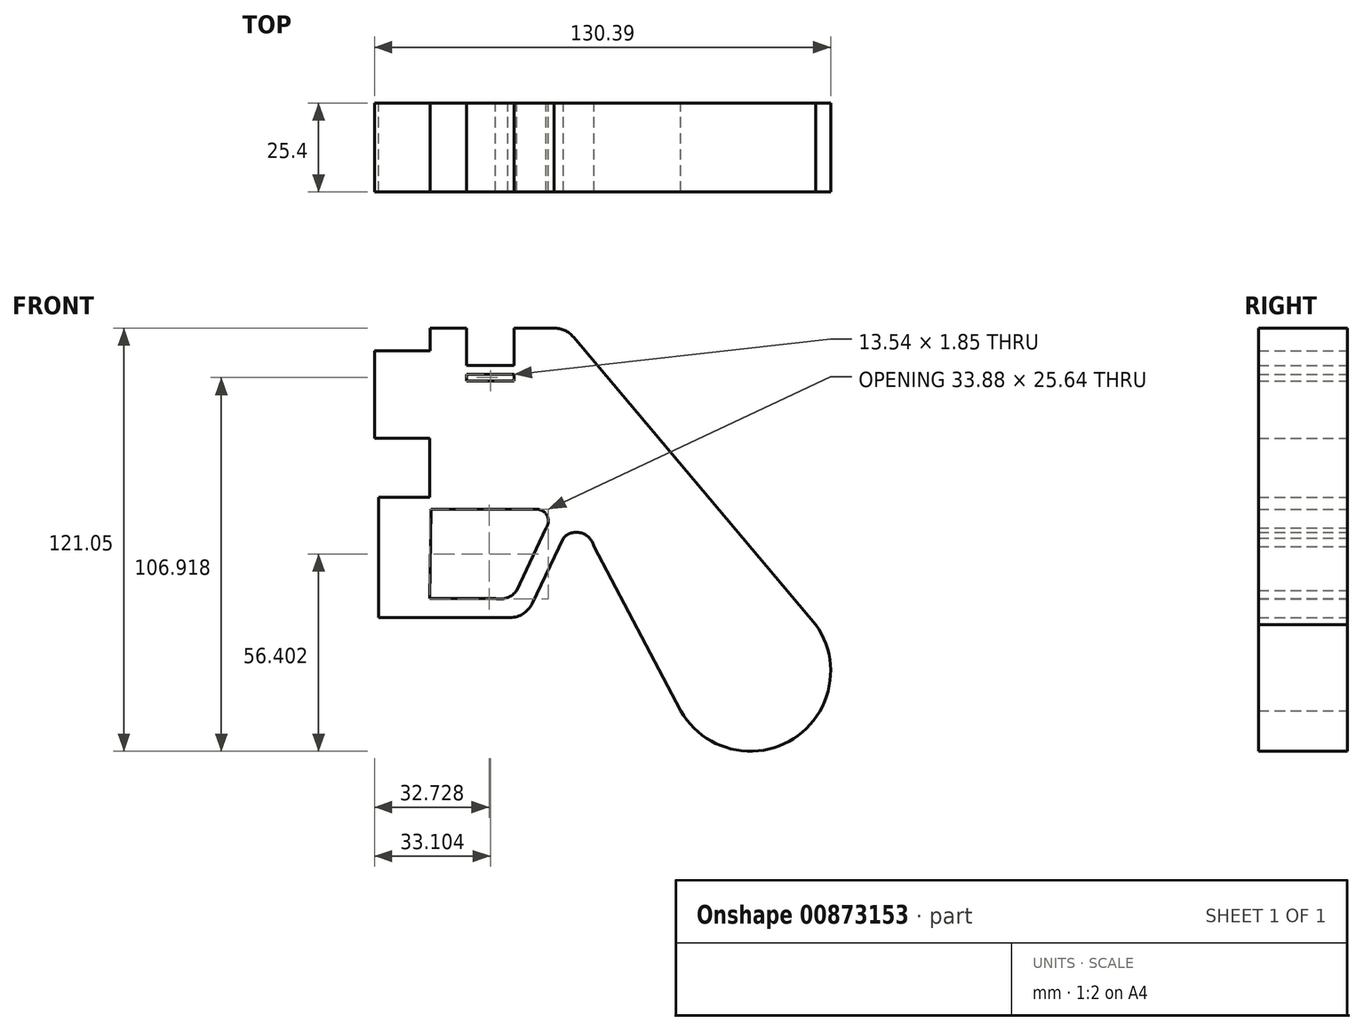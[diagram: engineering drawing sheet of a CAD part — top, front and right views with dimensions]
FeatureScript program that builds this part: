
annotation { "Feature Type Name" : "Feature", "Feature Type Description" : "" }
export const myFeature = defineFeature(function(context is Context, id is Id, definition is map)
    precondition{}
    {
        {
            var Q0;
            Q0=qCreatedBy(makeId("Front.planeOp"),FACE);
            var sketch = newSketch(context, id + "F0", { "sketchPlane" : qUnion([Q0])});
            skLineSegment(sketch, "E0", {"start": v(-46.23, 60.03) * mm, "end": v(-35.73, 60.03) * mm});
            skLineSegment(sketch, "E1", {"start": v(-35.73, 60.03) * mm, "end": v(-35.73, 44.97) * mm});
            skLineSegment(sketch, "E2", {"start": v(-35.73, 44.97) * mm, "end": v(-22.18, 44.97) * mm});
            skLineSegment(sketch, "E3", {"start": v(-22.18, 44.97) * mm, "end": v(-22.18, 60.03) * mm});
            skLineSegment(sketch, "E4", {"start": v(-22.18, 60.03) * mm, "end": v(-10.8, 60.03) * mm});
            skLineSegment(sketch, "E5", {"start": v(-5.22, 57.5) * mm, "end": v(64.06, -24.74) * mm});
            skLineSegment(sketch, "E6", {"start": v(0.63, -2.44) * mm, "end": v(25.46, -49.47) * mm});
            skLineSegment(sketch, "E7", {"start": v(-46.27, -17.3) * mm, "end": v(-27.53, -17.3) * mm});
            skLineSegment(sketch, "E8", {"start": v(-21.38, -15) * mm, "end": v(-13.09, 2.83) * mm});
            skLineSegment(sketch, "E9", {"start": v(-45.96, 8.2) * mm, "end": v(-15.7, 8.2) * mm});
            skArc(sketch, "E10", {"start": v(-13.09, 2.83) * mm, "mid": v(-12.7, 6.33) * mm, "end": v(-15.7, 8.2) * mm});
            skArc(sketch, "E11", {"start": v(-27.53, -17.3) * mm, "mid": v(-24.1, -17.07) * mm, "end": v(-21.38, -15) * mm});
            skLineSegment(sketch, "E12", {"start": v(-46.33, -22.77) * mm, "end": v(-23.96, -22.77) * mm});
            skLineSegment(sketch, "E13", {"start": v(-16.97, -18.72) * mm, "end": v(-8.13, 0) * mm});
            skArc(sketch, "E14", {"start": v(-23.96, -22.77) * mm, "mid": v(-19.83, -21.83) * mm, "end": v(-16.97, -18.72) * mm});
            skArc(sketch, "E15", {"start": v(0.63, -2.44) * mm, "mid": v(-3.01, 1.43) * mm, "end": v(-8.13, 0) * mm});
            skArc(sketch, "E16", {"start": v(25.46, -49.47) * mm, "mid": v(57.75, -57.4) * mm, "end": v(64.06, -24.74) * mm});
            skArc(sketch, "E17", {"start": v(-5.22, 57.5) * mm, "mid": v(-7.72, 59.4) * mm, "end": v(-10.8, 60.03) * mm});
            skLineSegment(sketch, "E18", {"start": v(-46.33, -22.77) * mm, "end": v(-46.32, -11.47) * mm});
            skLineSegment(sketch, "E19", {"start": v(-35.73, 49.36) * mm, "end": v(-22.18, 49.36) * mm});
            skLineSegment(sketch, "E20.0", {"start": v(-35.73, 46.82) * mm, "end": v(-22.18, 46.82) * mm});
            skLineSegment(sketch, "E21", {"start": v(-45.96, 8.2) * mm, "end": v(-46.27, -17.3) * mm});
            skLineSegment(sketch, "E22", {"start": v(-46.33, -22.77) * mm, "end": v(-60.93, -22.75) * mm});
            skLineSegment(sketch, "E23", {"start": v(-60.93, -22.75) * mm, "end": v(-60.93, -11.47) * mm});
            skLineSegment(sketch, "E24", {"start": v(-46.3, 11.67) * mm, "end": v(-60.93, 11.68) * mm});
            skLineSegment(sketch, "E25", {"start": v(-60.93, 11.68) * mm, "end": v(-60.93, -12.88) * mm});
            skLineSegment(sketch, "E26", {"start": v(-46.24, 53.54) * mm, "end": v(-62.06, 53.56) * mm});
            skLineSegment(sketch, "E27", {"start": v(-62.06, 53.56) * mm, "end": v(-62.06, 28.52) * mm});
            skLineSegment(sketch, "E28", {"start": v(-62.06, 28.52) * mm, "end": v(-46.27, 28.52) * mm});
            skLineSegment(sketch, "E29.trimOffspring", {"start": v(-46.24, 53.54) * mm, "end": v(-46.23, 60.03) * mm});
            skLineSegment(sketch, "E30.trimOffspring", {"start": v(-46.3, 11.67) * mm, "end": v(-46.27, 28.52) * mm});
            skSolve(sketch);
        }
        {
            var Q0;
            Q0 = qSketchRegion(id + "F0", true);
            extrude(context, id + "F1", {"entities" : qUnion([Q0]), "depth" : 14.48 * mm, "offsetDistance" : 25.4 * mm});
        }
        {
            var Q0;
            Q0 = qSketchRegion(id + "F0", true);
            extrude(context, id + "F2", {"entities" : qUnion([Q0]), "operationType" : NewBodyOperationType.ADD, "depth" : 25.4 * mm, "offsetDistance" : 25.4 * mm});
        }
        {
            var Q0;
            {var subQ0=sQuery(id+"F0.wireOp",EDGE,"E19");Q0=makeQuery(id+"F0.imprint","IMPRINT",FACE,{"disambiguationData":[TD([[makeQuery(id+"F0.imprint","IMPRINT",EDGE,{"derivedFrom":subQ0}),-1.0]])]});}
            extrude(context, id + "F3", {"entities" : qUnion([Q0]), "operationType" : NewBodyOperationType.ADD, "depth" : 15.24 * mm, "offsetDistance" : 25.4 * mm});
        }
    });
